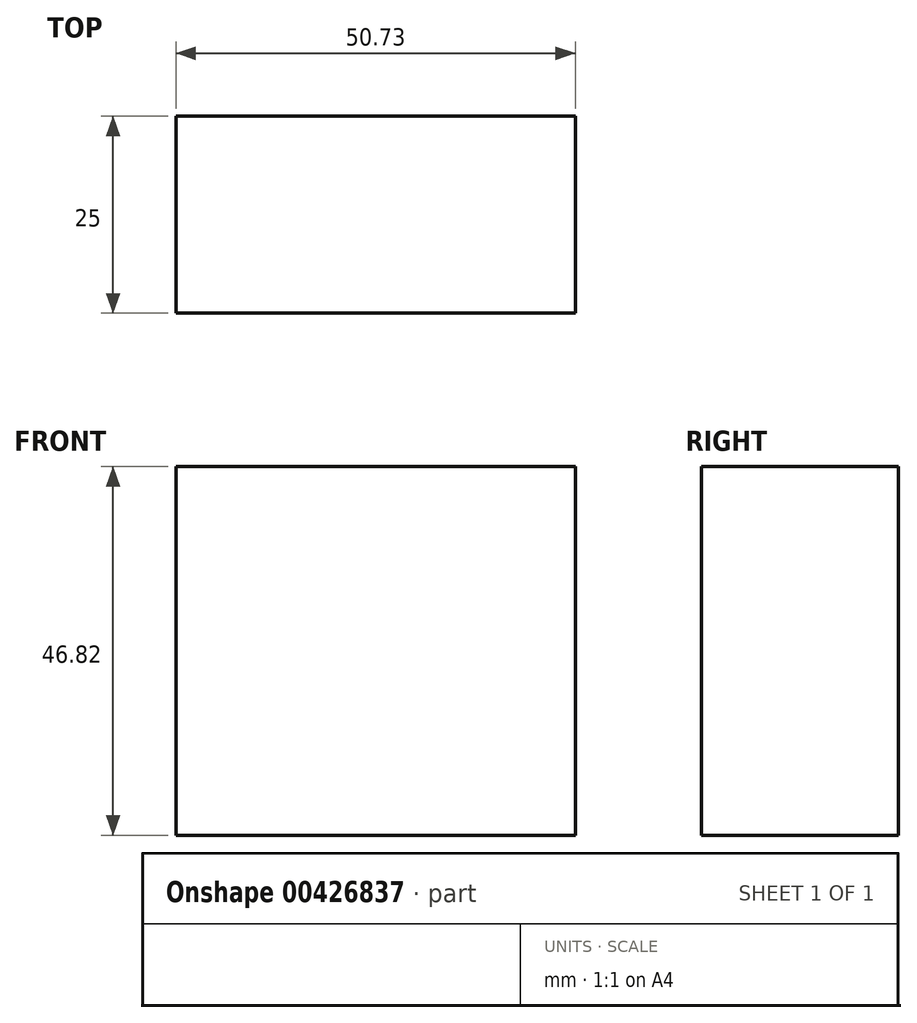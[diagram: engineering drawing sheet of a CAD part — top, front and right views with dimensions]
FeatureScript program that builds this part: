
annotation { "Feature Type Name" : "Feature", "Feature Type Description" : "" }
export const myFeature = defineFeature(function(context is Context, id is Id, definition is map)
    precondition{}
    {
        {
            var Q0;
            Q0=qCreatedBy(makeId("Front.planeOp"),FACE);
            var sketch = newSketch(context, id + "F0", { "sketchPlane" : qUnion([Q0])});
            skLineSegment(sketch, "E0.bottom", {"start": v(-123.5, 0) * mm, "end": v(-72.77, 0) * mm});
            skLineSegment(sketch, "E0.top", {"start": v(-123.5, 46.82) * mm, "end": v(-72.77, 46.82) * mm});
            skLineSegment(sketch, "E0.left", {"start": v(-123.5, 0) * mm, "end": v(-123.5, 46.82) * mm});
            skLineSegment(sketch, "E0.right", {"start": v(-72.77, 0) * mm, "end": v(-72.77, 46.82) * mm});
            skPoint(sketch, "E0.middle", {"position": v(-98.13, 23.4) * mm});
            skSolve(sketch);
        }
        {
            var Q0;
            Q0=makeQuery(id+"F0.imprint","IMPRINT",FACE,{"disambiguationData":[TD([[makeQuery(id+"F0.imprint","IMPRINT",EDGE,{"derivedFrom":sQuery(id+"F0.wireOp",EDGE,"E0.bottom")}),1.0]])]});
            extrude(context, id + "F1", {"entities" : qUnion([Q0]), "depth" : 25 * mm});
        }
    });
